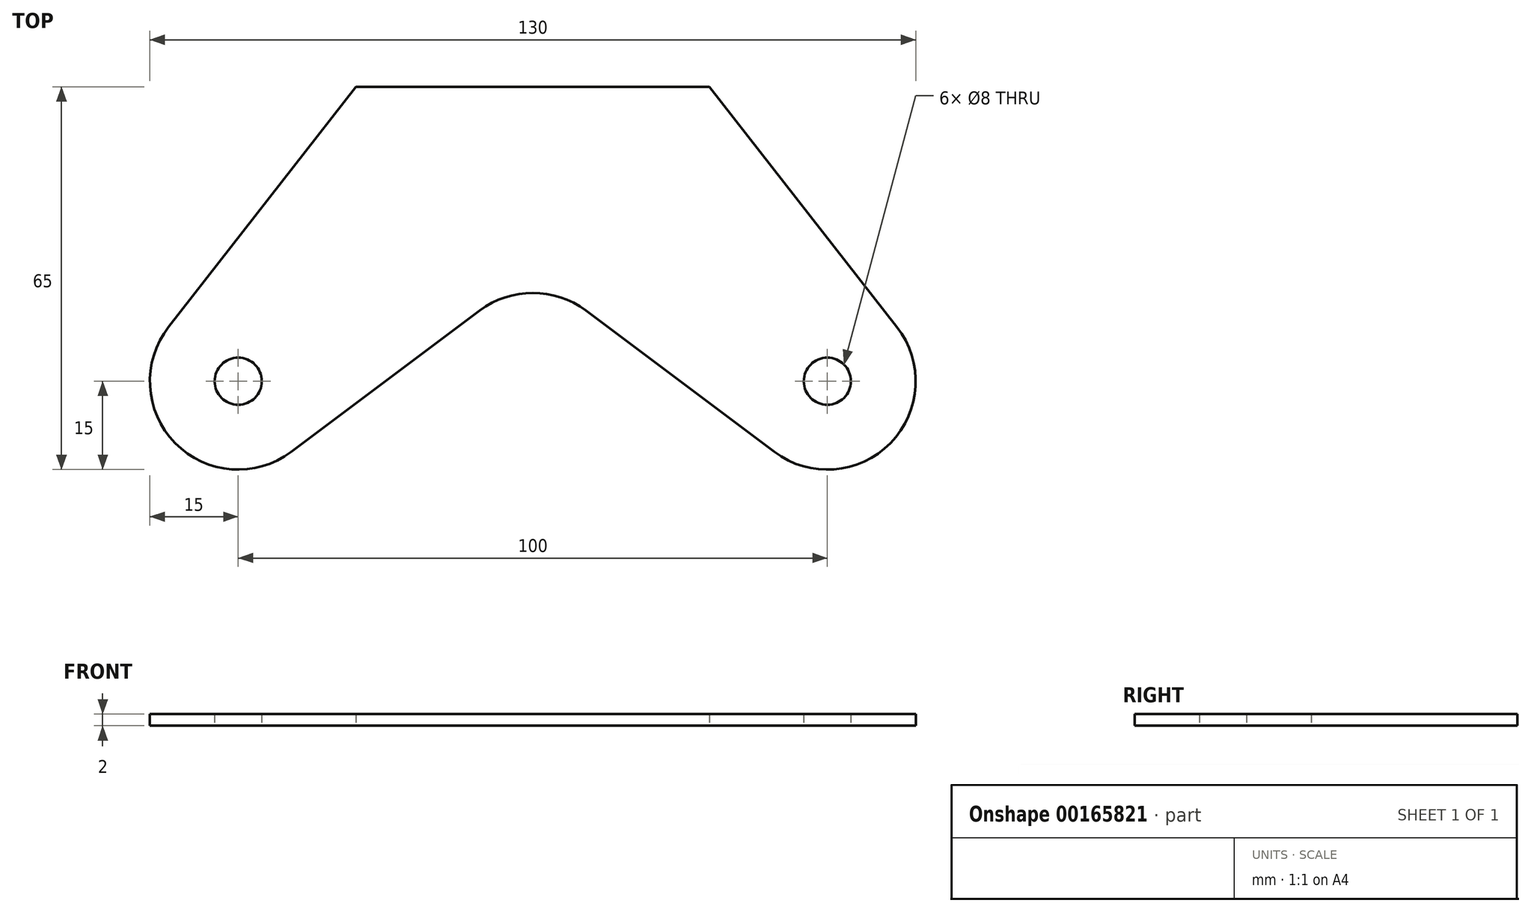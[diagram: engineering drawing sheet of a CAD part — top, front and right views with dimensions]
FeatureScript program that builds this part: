
annotation { "Feature Type Name" : "Feature", "Feature Type Description" : "" }
export const myFeature = defineFeature(function(context is Context, id is Id, definition is map)
    precondition{}
    {
        {
            var Q0;
            Q0=qCreatedBy(makeId("Top.planeOp"),FACE);
            var sketch = newSketch(context, id + "F0", { "sketchPlane" : qUnion([Q0])});
            skCircle(sketch, "E0", {"center": v(-50, 0) * mm, "radius": 4 * mm});
            skCircle(sketch, "E1", {"center": v(50, 0) * mm, "radius": 4 * mm});
            skLineSegment(sketch, "E2", {"start": v(-50, 0) * mm, "end": v(50, 0) * mm, "construction": true});
            skArc(sketch, "E3", {"start": v(-61.82, 9.23) * mm, "mid": v(-60.7, -10.5) * mm, "end": v(-41, -12) * mm});
            skArc(sketch, "E4", {"start": v(41, -12) * mm, "mid": v(60.7, -10.5) * mm, "end": v(61.82, 9.23) * mm});
            skArc(sketch, "E5", {"start": v(9, 12) * mm, "mid": v(0, 15) * mm, "end": v(-9, 12) * mm});
            skLineSegment(sketch, "E6", {"start": v(-41, -12) * mm, "end": v(-9, 12) * mm});
            skLineSegment(sketch, "E7", {"start": v(9, 12) * mm, "end": v(41, -12) * mm});
            skLineSegment(sketch, "E8", {"start": v(-30, 50) * mm, "end": v(30, 50) * mm});
            skLineSegment(sketch, "E9", {"start": v(30, 50) * mm, "end": v(61.82, 9.23) * mm});
            skLineSegment(sketch, "E10", {"start": v(-30, 50) * mm, "end": v(-61.82, 9.23) * mm});
            skLineSegment(sketch, "E11", {"start": v(0, 0) * mm, "end": v(0, 50) * mm, "construction": true});
            skSolve(sketch);
        }
        {
            var Q0;
            Q0=makeQuery(id+"F0.imprint","IMPRINT",FACE,{"disambiguationData":[TD([[makeQuery(id+"F0.imprint","IMPRINT",EDGE,{"derivedFrom":sQuery(id+"F0.wireOp",EDGE,"E0")}),-1.0]])]});
            extrude(context, id + "F1", {"entities" : qUnion([Q0]), "depth" : 2 * mm});
        }
    });
